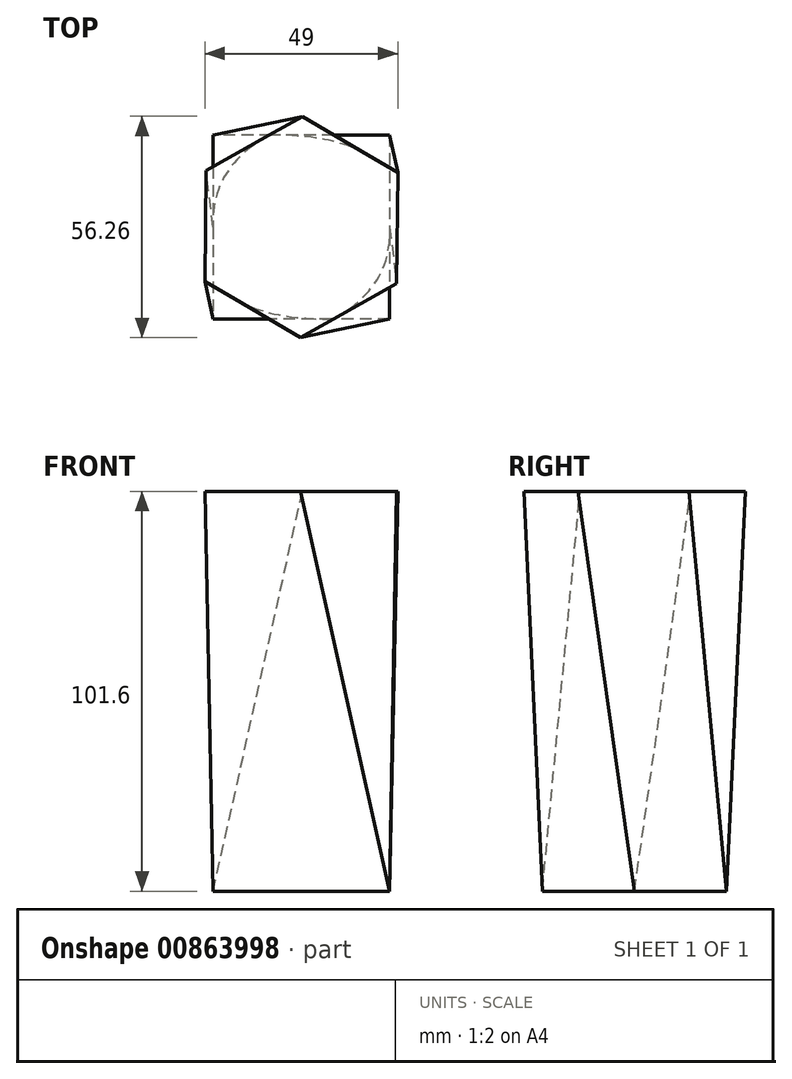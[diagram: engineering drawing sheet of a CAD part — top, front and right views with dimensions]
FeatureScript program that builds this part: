
annotation { "Feature Type Name" : "Feature", "Feature Type Description" : "" }
export const myFeature = defineFeature(function(context is Context, id is Id, definition is map)
    precondition{}
    {
        {
            var Q0;
            Q0=qCreatedBy(makeId("Top.planeOp"),FACE);
            var sketch = newSketch(context, id + "F0", { "sketchPlane" : qUnion([Q0])});
            skLineSegment(sketch, "E0.bottom", {"start": v(22.43, 23.4) * mm, "end": v(-22.43, 23.4) * mm});
            skLineSegment(sketch, "E0.top", {"start": v(22.43, -23.4) * mm, "end": v(-22.43, -23.4) * mm});
            skLineSegment(sketch, "E0.left", {"start": v(22.43, 23.4) * mm, "end": v(22.43, -23.4) * mm});
            skLineSegment(sketch, "E0.right", {"start": v(-22.43, 23.4) * mm, "end": v(-22.43, -23.4) * mm});
            skPoint(sketch, "E0.middle", {"position": v(0, 0) * mm});
            skSolve(sketch);
        }
        {
            var Q0;
            Q0=qCreatedBy(makeId("Top.planeOp"),FACE);
            cPlane(context, id + "F1", {"entities" : qUnion([Q0]), "cplaneType" : CPlaneType.OFFSET, "offset" : 76.2 * mm, "width" : 152.4 * mm, "height" : 152.4 * mm});
        }
        {
            var Q0;
            Q0=qCreatedBy(id+"F1.planeOp",FACE);
            cPlane(context, id + "F2", {"entities" : qUnion([Q0]), "cplaneType" : CPlaneType.OFFSET, "offset" : 25.4 * mm, "width" : 152.4 * mm, "height" : 152.4 * mm});
        }
        {
            var Q0;
            Q0=qCreatedBy(id+"F2.planeOp",FACE);
            var sketch = newSketch(context, id + "F3", { "sketchPlane" : qUnion([Q0])});
            skCircle(sketch, "E1.cCircle", {"center": v(0, 0) * mm, "radius": 24.36 * mm, "construction": true});
            skLineSegment(sketch, "E1.0", {"start": v(0.28, 28.13) * mm, "end": v(24.5, 13.82) * mm});
            skLineSegment(sketch, "E1.1", {"start": v(24.5, 13.82) * mm, "end": v(24.22, -14.3) * mm});
            skLineSegment(sketch, "E1.2", {"start": v(24.22, -14.3) * mm, "end": v(-0.28, -28.13) * mm});
            skLineSegment(sketch, "E1.3", {"start": v(-0.28, -28.13) * mm, "end": v(-24.5, -13.82) * mm});
            skLineSegment(sketch, "E1.4", {"start": v(-24.5, -13.82) * mm, "end": v(-24.22, 14.3) * mm});
            skLineSegment(sketch, "E1.5", {"start": v(-24.22, 14.3) * mm, "end": v(0.28, 28.13) * mm});
            skPoint(sketch, "E1.0.midPoint", {"position": v(12.4, 20.97) * mm});
            skSolve(sketch);
        }
        {
            var Q0;
            Q0=makeQuery(id+"F0.imprint","IMPRINT",FACE,{"disambiguationData":[TD([[makeQuery(id+"F0.imprint","IMPRINT",EDGE,{"derivedFrom":sQuery(id+"F0.wireOp",EDGE,"E0.bottom")}),1.0]])]});
            var Q1;
            Q1=makeQuery(id+"F3.imprint","IMPRINT",FACE,{"disambiguationData":[TD([[makeQuery(id+"F3.imprint","IMPRINT",EDGE,{"derivedFrom":sQuery(id+"F3.wireOp",EDGE,"E1.0")}),-1.0]])]});
            loft(context, id + "F4", {"sheetProfilesArray" : [{ "sheetProfileEntities" : qUnion([Q0]) }, { "sheetProfileEntities" : qUnion([Q1]) }]});
        }
    });
